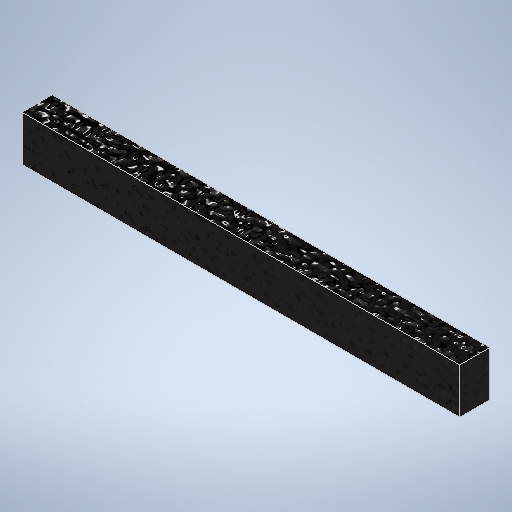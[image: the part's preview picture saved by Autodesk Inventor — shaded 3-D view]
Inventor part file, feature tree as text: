
AUTODESK INVENTOR PART (.ipt)
format: ipt  version: 2025 (Build 290162010, 162A)  size: 272,384 bytes
history: native  units: in
note: dims shown in document units (in); Inventor stores cm internally (conversion verified against a paired STEP export)
features: extrude x1, sketch x1
ambient origin geometry x8: Origin, YZ Plane, XZ Plane, XY Plane, X Axis, Y Axis, Z Axis, Center Point
bodies: Solid1 (feature_tree)
feature tree (2):
  extrude  "Extrusion1"  Depth=14.5in
  sketch  "Sketch1"  dims[d2=1.5in d3=14.5in d4=1.0in d5=0.0in]
